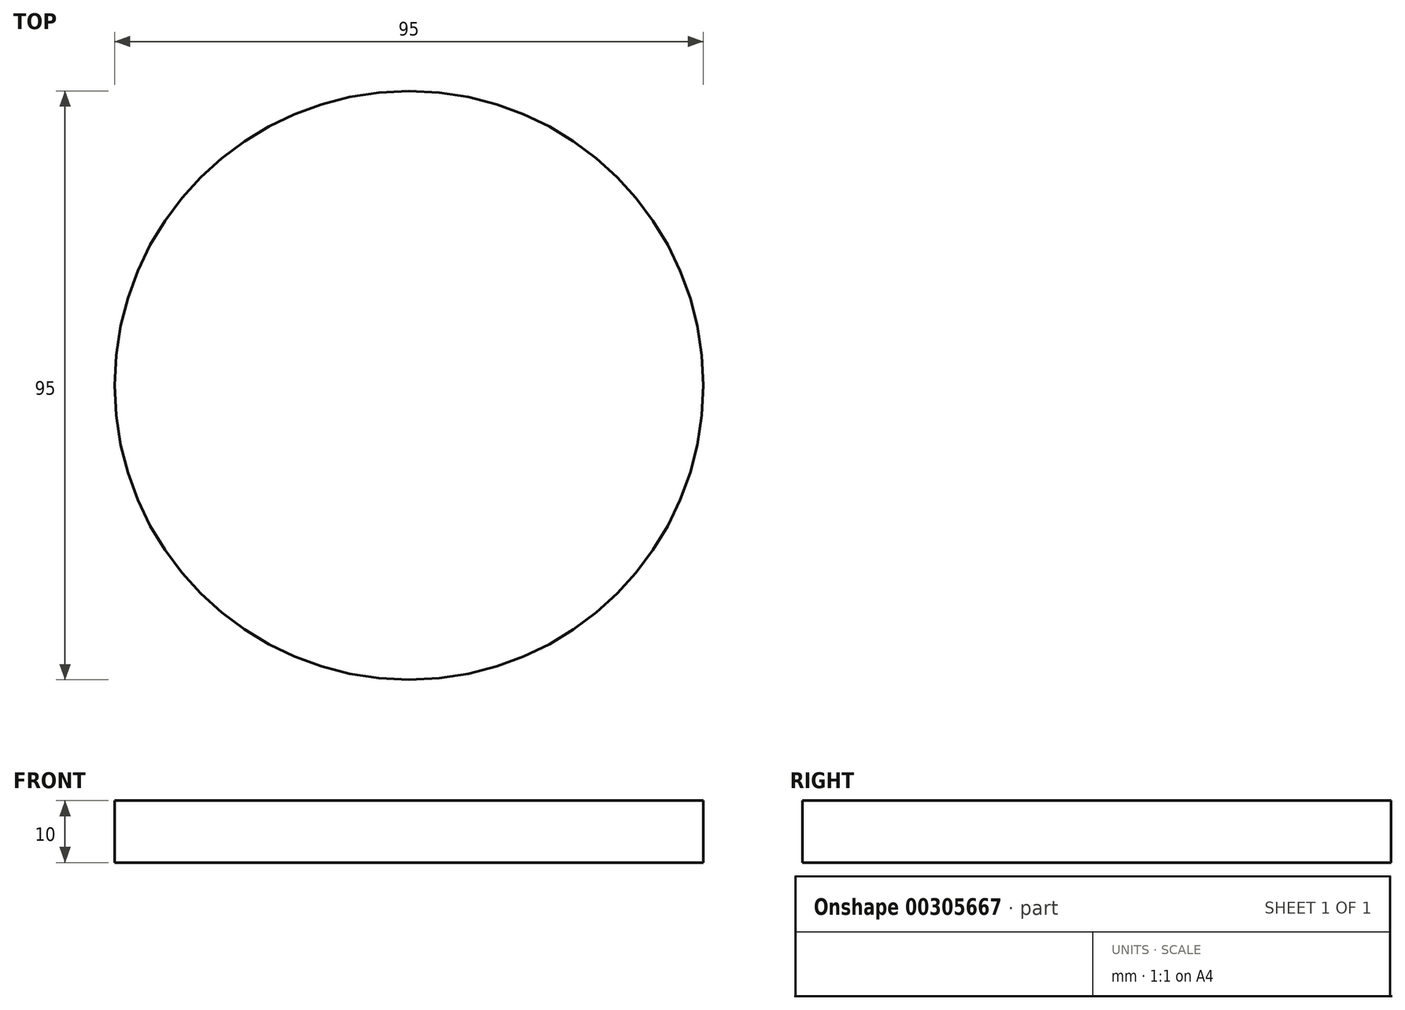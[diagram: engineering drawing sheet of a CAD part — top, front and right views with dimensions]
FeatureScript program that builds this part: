
annotation { "Feature Type Name" : "Feature", "Feature Type Description" : "" }
export const myFeature = defineFeature(function(context is Context, id is Id, definition is map)
    precondition{}
    {
        {
            var Q0;
            Q0=qCreatedBy(makeId("Top.planeOp"),FACE);
            var sketch = newSketch(context, id + "F0", { "sketchPlane" : qUnion([Q0])});
            skCircle(sketch, "E0", {"center": v(0, 0) * mm, "radius": 47.5 * mm});
            skLineSegment(sketch, "E1", {"start": v(0, 59.12) * mm, "end": v(0, -74.03) * mm, "construction": true});
            skLineSegment(sketch, "E2", {"start": v(-79.52, 0) * mm, "end": v(85.22, 0) * mm, "construction": true});
            skSolve(sketch);
        }
        {
            var Q0;
            Q0 = qSketchRegion(id + "F0", true);
            extrude(context, id + "F1", {"entities" : qUnion([Q0]), "endBound" : BoundingType.SYMMETRIC, "depth" : 10 * mm, "offsetDistance" : 25 * mm});
        }
        {
            var Q0;
            Q0=qCreatedBy(makeId("Front.planeOp"),FACE);
            cPlane(context, id + "F2", {"entities" : qUnion([Q0]), "cplaneType" : CPlaneType.OFFSET, "offset" : (95 / 2) * mm, "width" : 150 * mm, "height" : 150 * mm});
        }
    });
